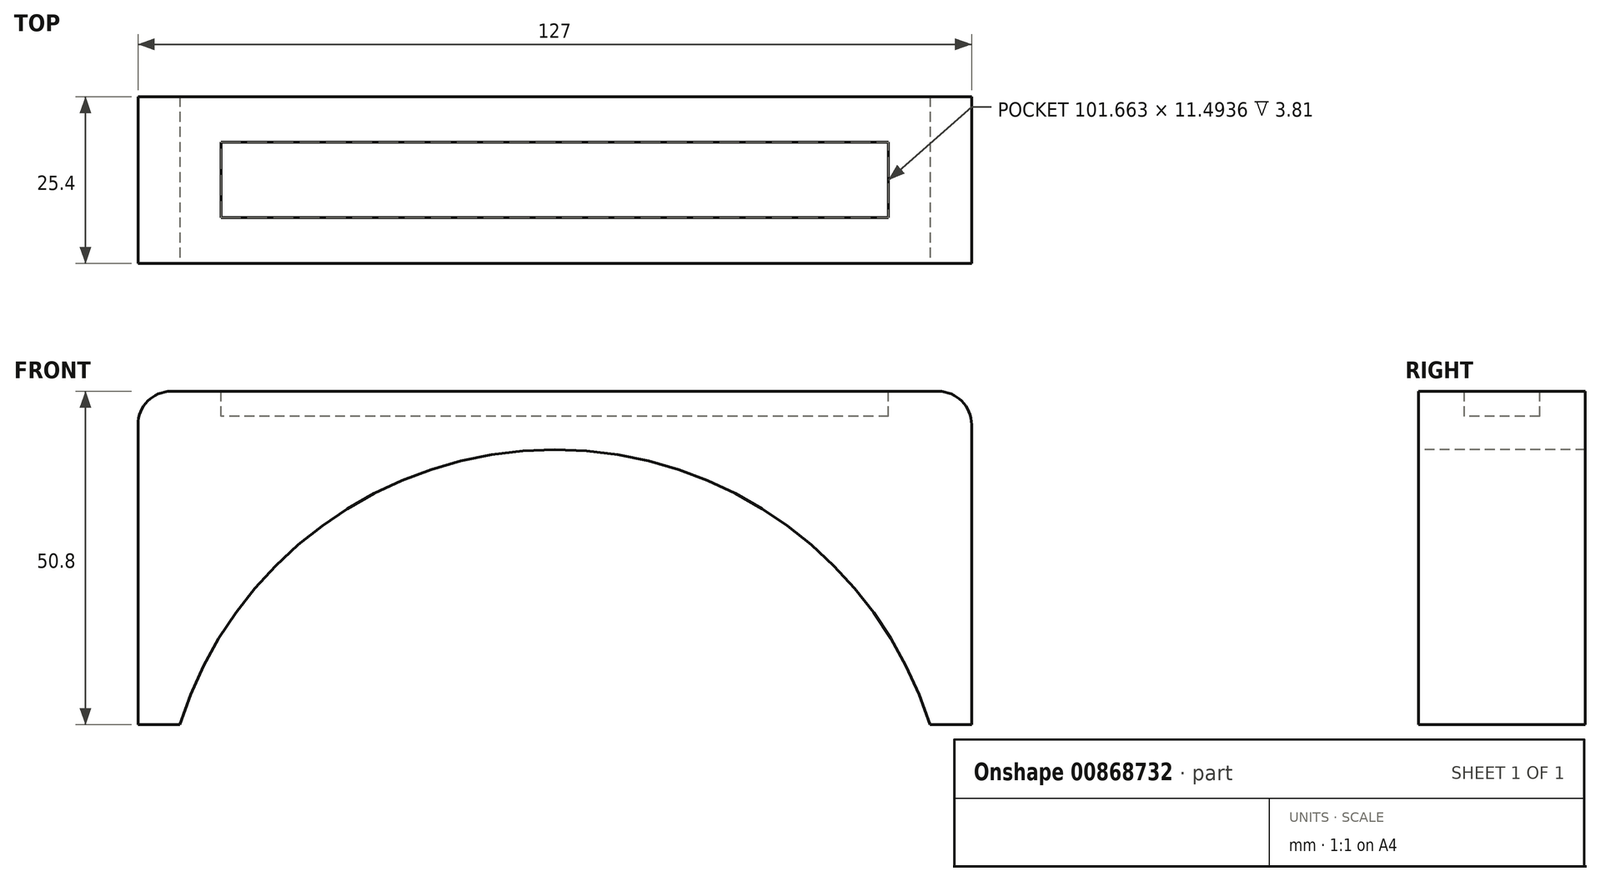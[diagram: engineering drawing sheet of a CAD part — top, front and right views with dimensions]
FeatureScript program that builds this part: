
annotation { "Feature Type Name" : "Feature", "Feature Type Description" : "" }
export const myFeature = defineFeature(function(context is Context, id is Id, definition is map)
    precondition{}
    {
        {
            var Q0;
            Q0=qCreatedBy(makeId("Top.planeOp"),FACE);
            var sketch = newSketch(context, id + "F0", { "sketchPlane" : qUnion([Q0])});
            skLineSegment(sketch, "E0.bottom", {"start": v(63.5, 12.7) * mm, "end": v(-63.5, 12.7) * mm});
            skLineSegment(sketch, "E0.top", {"start": v(63.5, -12.7) * mm, "end": v(-63.5, -12.7) * mm});
            skLineSegment(sketch, "E0.left", {"start": v(63.5, 12.7) * mm, "end": v(63.5, -12.7) * mm});
            skLineSegment(sketch, "E0.right", {"start": v(-63.5, 12.7) * mm, "end": v(-63.5, -12.7) * mm});
            skPoint(sketch, "E0.middle", {"position": v(0, 0) * mm});
            skSolve(sketch);
        }
        {
            var Q0;
            Q0=makeQuery(id+"F0.imprint","IMPRINT",FACE,{"disambiguationData":[TD([[makeQuery(id+"F0.imprint","IMPRINT",EDGE,{"derivedFrom":sQuery(id+"F0.wireOp",EDGE,"E0.bottom")}),1.0]])]});
            extrude(context, id + "F1", {"entities" : qUnion([Q0]), "depth" : 50.8 * mm, "offsetDistance" : 25.4 * mm});
        }
        {
            var Q0;
            Q0=makeQuery(id+"F1.opExtrude","CAP_FACE",FACE,{"disambiguationData":[OSD([sQuery(id+"F0.wireOp",EDGE,"E0.bottom"),sQuery(id+"F0.wireOp",EDGE,"E0.top"),sQuery(id+"F0.wireOp",EDGE,"E0.left"),sQuery(id+"F0.wireOp",EDGE,"E0.right")])],"isStart":false});
            var sketch = newSketch(context, id + "F2", { "sketchPlane" : qUnion([Q0])});
            skLineSegment(sketch, "E1.bottom", {"start": v(50.83, 5.75) * mm, "end": v(-50.83, 5.75) * mm});
            skLineSegment(sketch, "E1.top", {"start": v(50.83, -5.75) * mm, "end": v(-50.83, -5.75) * mm});
            skLineSegment(sketch, "E1.left", {"start": v(50.83, 5.75) * mm, "end": v(50.83, -5.75) * mm});
            skLineSegment(sketch, "E1.right", {"start": v(-50.83, 5.75) * mm, "end": v(-50.83, -5.75) * mm});
            skPoint(sketch, "E1.middle", {"position": v(0, 0) * mm});
            skSolve(sketch);
        }
        {
            var Q0;
            Q0=makeQuery(id+"F2.imprint","IMPRINT",FACE,{"disambiguationData":[TD([[makeQuery(id+"F2.imprint","IMPRINT",EDGE,{"derivedFrom":sQuery(id+"F2.wireOp",EDGE,"E1.bottom")}),1.0]])]});
            extrude(context, id + "F3", {"entities" : qUnion([Q0]), "operationType" : NewBodyOperationType.REMOVE, "oppositeDirection" : true, "depth" : 3.8 * mm, "offsetDistance" : 25.4 * mm});
        }
        {
            var Q0;
            Q0=makeQuery(id+"F1.opExtrude","SWEPT_FACE",FACE,{"disambiguationData":[OSD([sQuery(id+"F0.wireOp",EDGE,"E0.top")])]});
            var sketch = newSketch(context, id + "F4", { "sketchPlane" : qUnion([Q0])});
            skLineSegment(sketch, "E2", {"start": v(0, 0) * mm, "end": v(-57.15, 0) * mm, "construction": true});
            skLineSegment(sketch, "E3.MirrorCS", {"start": v(0, 0) * mm, "end": v(57.15, 0) * mm, "construction": true});
            skLineSegment(sketch, "E4", {"start": v(0, 50.8) * mm, "end": v(0, 41.91) * mm, "construction": true});
            skArc(sketch, "E5", {"start": v(57.15, 0) * mm, "mid": v(0, 41.91) * mm, "end": v(-57.15, 0) * mm});
            skLineSegment(sketch, "E6", {"start": v(-57.15, 0) * mm, "end": v(57.15, 0) * mm});
            skSolve(sketch);
        }
        {
            var Q0;
            Q0=makeQuery(id+"F4.imprint","IMPRINT",FACE,{"disambiguationData":[TD([[makeQuery(id+"F4.imprint","IMPRINT",EDGE,{"derivedFrom":sQuery(id+"F4.wireOp",EDGE,"E5")}),1.0]])]});
            extrude(context, id + "F5", {"entities" : qUnion([Q0]), "operationType" : NewBodyOperationType.REMOVE, "oppositeDirection" : true, "depth" : 50.8 * mm, "offsetDistance" : 25.4 * mm});
        }
        {
            var Q0;
            Q0=makeQuery(id+"F1.opExtrude","CAP_EDGE",EDGE,{"disambiguationData":[OSD([sQuery(id+"F0.wireOp",EDGE,"E0.right")])],"isStart":false});
            var Q1;
            Q1=makeQuery(id+"F1.opExtrude","CAP_EDGE",EDGE,{"disambiguationData":[OSD([sQuery(id+"F0.wireOp",EDGE,"E0.left")])],"isStart":false});
            fillet(context, id + "F6", {"entities" : qUnion([Q0, Q1]), "radius" : 5.08 * mm, "tangentPropagation" : true, "allowEdgeOverflow" : false});
        }
    });
